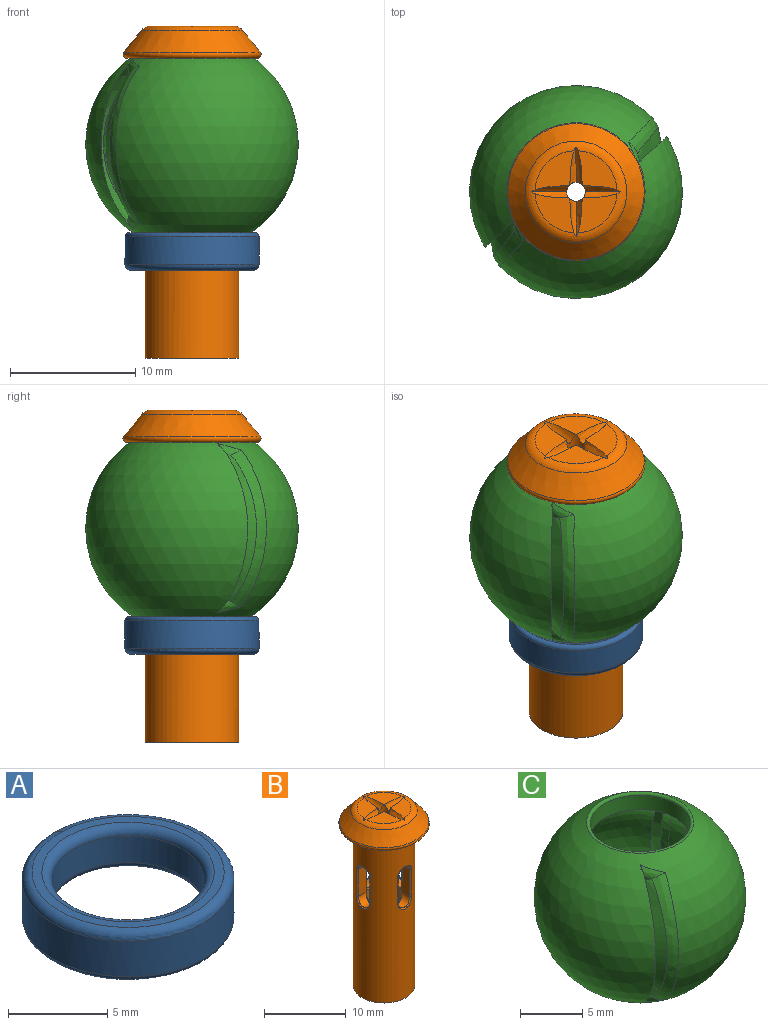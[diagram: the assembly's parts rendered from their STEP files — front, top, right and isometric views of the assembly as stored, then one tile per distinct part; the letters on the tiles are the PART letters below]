
ASSEMBLY  parts=3 mates=2
PART A: 8 faces, bbox 11.6x11.6x3 mm
  f0: cone r=4.03mm half-angle=60deg, axis (0,0,-1), area 28.1mm2, adj f1,f5
  f1: torus R=4.22mm, axis (0,0,1), area 9.5mm2, adj f0,f2
  f2: cylinder r=3.85mm len=7.7mm, axis (0,0,1), area 39.7mm2, adj f1,f6
  f3: plane 9.7x9.7mm, normal (0,0,1), area 14.5mm2, adj f6,f7
  f4: cylinder r=5.35mm len=10.7mm, axis (0,0,1), area 74mm2, adj f5,f7
  f5: torus R=5.05mm, axis (0,0,1), area 20.4mm2, adj f0,f4
  f6: torus R=4.35mm, axis (0,0,-1), area 19.9mm2, adj f2,f3
  f7: torus R=4.85mm, axis (0,0,-1), area 25.5mm2, adj f3,f4
PART B: 70 faces, bbox 11.9x11.9x27.5 mm
  f0: plane 3.11x3.11mm, normal (0,0,1), area 6mm2, adj f7,f8,f20,f69
  f1: plane 3.11x3.11mm, normal (0,0,1), area 6mm2, adj f5,f6,f20,f69
  f2: plane 3.11x3.11mm, normal (0,0,1), area 6mm2, adj f4,f11,f20,f69
  f3: sphere r=2.25mm, area 30mm2, adj f15,f20
  f4: torus R=7.85mm, axis (1,0,0), area 1.8mm2, adj f2,f5,f20,f69
  f5: torus R=7.85mm, axis (1,0,0), area 1.8mm2, adj f1,f4,f20,f69
  f6: torus R=7.85mm, axis (0,-1,0), area 1.8mm2, adj f1,f7,f20,f69
  f7: torus R=7.85mm, axis (0,-1,0), area 1.8mm2, adj f0,f6,f20,f69
  f8: torus R=7.85mm, axis (-1,0,0), area 1.8mm2, adj f0,f9,f20,f69
  f9: torus R=7.85mm, axis (-1,0,0), area 1.8mm2, adj f8,f16,f20,f69
  f10: torus R=7.85mm, axis (0,1,0), area 1.8mm2, adj f11,f16,f20,f69
  f11: torus R=7.85mm, axis (0,1,0), area 1.8mm2, adj f2,f10,f20,f69
  f12: torus R=4.05mm, axis (0,0,1), area 15.5mm2, adj f13,f19
  f13: cylinder r=3.75mm len=24.21mm, axis (0,0,1), area 513.8mm2, adj f12,f14,f25,f26,f27,f28,f37,f38
  f14: plane 7.5x7.5mm, normal (0,0,-1), area 28.3mm2, adj f13,f15
  f15: cylinder r=2.25mm len=23.25mm, axis (0,0,1), area 276.6mm2, adj f3,f14,f29,f30,f31,f32,f41,f42
  f16: plane 3.11x3.11mm, normal (0,0,1), area 6mm2, adj f9,f10,f20,f69
  f17: cone r=5.45mm half-angle=39.2deg, axis (0,0,-1), area 66mm2, adj f18,f69
  f18: torus R=5.22mm, axis (0,0,1), area 28.2mm2, adj f17,f19
  f19: cone r=4.2mm half-angle=60deg, axis (0,0,-1), area 29.1mm2, adj f12,f18
  f20: cylinder r=0.75mm len=1.5mm, axis (0,0,-1), area 3.4mm2, adj f0,f1,f2,f3,f4,f5,f6,f7
  f21: cylinder r=1mm len=2mm, axis (0,-1,0), area 3.9mm2, adj f22,f24,f25,f29
  f22: plane 4x1.31mm, normal (1,0,0), area 5.2mm2, adj f21,f23,f27,f31
  f23: cylinder r=1mm len=2mm, axis (0,-1,0), area 3.9mm2, adj f22,f24,f28,f32
  f24: plane 4x1.31mm, normal (-1,0,0), area 5.2mm2, adj f21,f23,f26,f30
  f25: bspline ~2.4x1.4mm, area 0.9mm2, adj f13,f21,f26,f27
  f26: cylinder r=0.15mm len=4mm, axis (0,0,1), area 1.1mm2, adj f13,f24,f25,f28
  f27: cylinder r=0.15mm len=4mm, axis (0,0,1), area 1.1mm2, adj f13,f22,f25,f28
  f28: bspline ~2.4x1.4mm, area 0.9mm2, adj f13,f23,f26,f27
  f29: bspline ~2.16x1.38mm, area 0.7mm2, adj f15,f21,f30,f31
  f30: cylinder r=0.15mm len=4mm, axis (0,0,1), area 0.6mm2, adj f15,f24,f29,f32
  f31: cylinder r=0.15mm len=4mm, axis (0,0,1), area 0.6mm2, adj f15,f22,f29,f32
  f32: bspline ~2.16x1.38mm, area 0.7mm2, adj f15,f23,f30,f31
  f33: cylinder r=1mm len=2mm, axis (-1,0,0), area 3.9mm2, adj f34,f36,f37,f41
  f34: plane 4x1.31mm, normal (0,-1,0), area 5.2mm2, adj f33,f35,f39,f43
  f35: cylinder r=1mm len=2mm, axis (-1,0,0), area 3.9mm2, adj f34,f36,f40,f44
  f36: plane 4x1.31mm, normal (0,1,0), area 5.2mm2, adj f33,f35,f38,f42
  f37: bspline ~2.4x1.4mm, area 0.9mm2, adj f13,f33,f38,f39
  f38: cylinder r=0.15mm len=4mm, axis (0,0,1), area 1.1mm2, adj f13,f36,f37,f40
  f39: cylinder r=0.15mm len=4mm, axis (0,0,1), area 1.1mm2, adj f13,f34,f37,f40
  f40: bspline ~2.4x1.22mm, area 0.9mm2, adj f13,f35,f38,f39
  f41: bspline ~2.16x1.38mm, area 0.7mm2, adj f15,f33,f42,f43
  f42: cylinder r=0.15mm len=4mm, axis (0,0,1), area 0.6mm2, adj f15,f36,f41,f44
  f43: cylinder r=0.15mm len=4mm, axis (0,0,1), area 0.6mm2, adj f15,f34,f41,f44
  f44: bspline ~2.16x1.38mm, area 0.7mm2, adj f15,f35,f42,f43
  f45: cylinder r=1mm len=2mm, axis (0,1,0), area 3.9mm2, adj f46,f48,f49,f53
  f46: plane 4x1.31mm, normal (-1,0,0), area 5.2mm2, adj f45,f47,f51,f55
  f47: cylinder r=1mm len=2mm, axis (0,1,0), area 3.9mm2, adj f46,f48,f52,f56
  f48: plane 4x1.31mm, normal (1,0,0), area 5.2mm2, adj f45,f47,f50,f54
  f49: bspline ~2.4x1.4mm, area 0.9mm2, adj f13,f45,f50,f51
  f50: cylinder r=0.15mm len=4mm, axis (0,0,1), area 1.1mm2, adj f13,f48,f49,f52
  f51: cylinder r=0.15mm len=4mm, axis (0,0,1), area 1.1mm2, adj f13,f46,f49,f52
  f52: bspline ~2.4x1.4mm, area 0.9mm2, adj f13,f47,f50,f51
  f53: bspline ~2.16x1.38mm, area 0.7mm2, adj f15,f45,f54,f55
  f54: cylinder r=0.15mm len=4mm, axis (0,0,1), area 0.6mm2, adj f15,f48,f53,f56
  f55: cylinder r=0.15mm len=4mm, axis (0,0,1), area 0.6mm2, adj f15,f46,f53,f56
  f56: bspline ~2.16x1.38mm, area 0.7mm2, adj f15,f47,f54,f55
  f57: cylinder r=1mm len=2mm, axis (1,0,0), area 3.9mm2, adj f58,f60,f61,f65
  f58: plane 4x1.31mm, normal (0,1,0), area 5.2mm2, adj f57,f59,f63,f67
  f59: cylinder r=1mm len=2mm, axis (1,0,0), area 3.9mm2, adj f58,f60,f64,f68
  f60: plane 4x1.31mm, normal (0,-1,0), area 5.2mm2, adj f57,f59,f62,f66
  f61: bspline ~2.4x1.4mm, area 0.9mm2, adj f13,f57,f62,f63
  f62: cylinder r=0.15mm len=4mm, axis (0,0,1), area 1.1mm2, adj f13,f60,f61,f64
  f63: cylinder r=0.15mm len=4mm, axis (0,0,1), area 1.1mm2, adj f13,f58,f61,f64
  f64: bspline ~2.4x1.4mm, area 0.9mm2, adj f13,f59,f62,f63
  f65: bspline ~2.16x1.39mm, area 0.7mm2, adj f15,f57,f66,f67
  f66: cylinder r=0.15mm len=4mm, axis (0,0,1), area 0.6mm2, adj f15,f60,f65,f68
  f67: cylinder r=0.15mm len=4mm, axis (0,0,1), area 0.6mm2, adj f15,f58,f65,f68
  f68: bspline ~2.16x1.38mm, area 0.7mm2, adj f15,f59,f66,f67
  f69: torus R=3.28mm, axis (0,0,-1), area 20.4mm2, adj f0,f1,f2,f4,f5,f6,f7,f8
PART C: 35 faces, bbox 17x19.9x14.7 mm
  f0: sphere r=7mm, area 233.4mm2, adj f2,f3,f6,f7,f9,f10,f12,f29
  f1: sphere r=7mm, area 233.4mm2, adj f2,f3,f15,f16,f17,f20,f21,f23
  f2: cylinder r=4mm len=8mm, axis (0,0,-1), area 35.5mm2, adj f0,f1,f12,f15,f26,f29,f33
  f3: cylinder r=4mm len=8mm, axis (0,0,-1), area 35.5mm2, adj f0,f1,f10,f17,f24,f31,f34
  f4: sphere r=8.5mm, area 728.8mm2, adj f8,f13,f14,f18,f22,f27,f28,f32
  f5: bspline ~11.59x7.14mm, area 0mm2, adj f8,f12,f14,f15
  f6: bspline ~13.01x7.85mm, area 38.4mm2, adj f0,f7,f9,f13,f14,f18
  f7: bspline ~5.83x3.21mm, area 0.2mm2, adj f0,f6,f10,f13
  f8: bspline ~13.68x8.49mm, area 42mm2, adj f4,f5,f11,f13,f14,f16
  f9: bspline ~5.83x3.21mm, area 0.2mm2, adj f0,f6,f12,f14
  f10: bspline ~4.8x3.99mm, area 0.2mm2, adj f0,f3,f7,f11,f13,f17
  f11: bspline ~11.59x7.14mm, area 0mm2, adj f8,f10,f13,f17
  f12: bspline ~4.8x3.99mm, area 0.2mm2, adj f0,f2,f5,f9,f14,f15
  f13: bspline ~3.78x2.38mm, area 2.4mm2, adj f4,f6,f7,f8,f10,f11,f18
  f14: bspline ~4.53x2.99mm, area 2.4mm2, adj f4,f5,f6,f8,f9,f12,f18
  f15: bspline ~1.54x1.28mm, area 0.7mm2, adj f1,f2,f5,f12,f16
  f16: bspline ~11.12x2.76mm, area 9.4mm2, adj f1,f8,f15,f17
  f17: bspline ~1.54x1.28mm, area 0.7mm2, adj f1,f3,f10,f11,f16
  f18: bspline ~13.12x3.9mm, area 13.8mm2, adj f4,f6,f13,f14
  f19: bspline ~11.59x7.14mm, area 0mm2, adj f22,f26,f28,f29
  f20: bspline ~13.01x7.85mm, area 38.4mm2, adj f1,f21,f23,f27,f28,f32
  f21: bspline ~5.83x3.21mm, area 0.2mm2, adj f1,f20,f24,f27
  f22: bspline ~13.68x8.49mm, area 42mm2, adj f4,f19,f25,f27,f28,f30
  f23: bspline ~5.83x3.21mm, area 0.2mm2, adj f1,f20,f26,f28
  f24: bspline ~4.8x3.99mm, area 0.2mm2, adj f1,f3,f21,f25,f27,f31
  f25: bspline ~11.59x7.14mm, area 0mm2, adj f22,f24,f27,f31
  f26: bspline ~4.8x3.99mm, area 0.2mm2, adj f1,f2,f19,f23,f28,f29
  f27: bspline ~3.78x2.38mm, area 2.4mm2, adj f4,f20,f21,f22,f24,f25,f32
  f28: bspline ~4.53x2.99mm, area 2.4mm2, adj f4,f19,f20,f22,f23,f26,f32
  f29: bspline ~1.54x1.28mm, area 0.7mm2, adj f0,f2,f19,f26,f30
  f30: bspline ~11.12x2.76mm, area 9.4mm2, adj f0,f22,f29,f31
  f31: bspline ~1.54x1.28mm, area 0.7mm2, adj f0,f3,f24,f25,f30
  f32: bspline ~13.12x3.9mm, area 13.8mm2, adj f4,f20,f27,f28
  f33: torus R=4.2mm, axis (0,0,-1), area 10.9mm2, adj f2,f4
  f34: torus R=4.2mm, axis (0,0,1), area 10.9mm2, adj f3,f4
PLACE A rot(axis=(-0.97,-0.24,0),180deg) t=(8.77,6.06,7.83)mm
PLACE B t=(8.77,6.06,6.82)mm fixed
PLACE C rot(axis=(0,0,1),157.9deg) t=(8.77,6.06,7.37)mm
MATE cylindrical B.f12 <-> C.f2  axis (0,0,1) through (8.77,6.06,2.42)mm
MATE cylindrical B.f12 <-> A.f2  axis (0,0,-1) through (8.77,6.06,-9.68)mm
